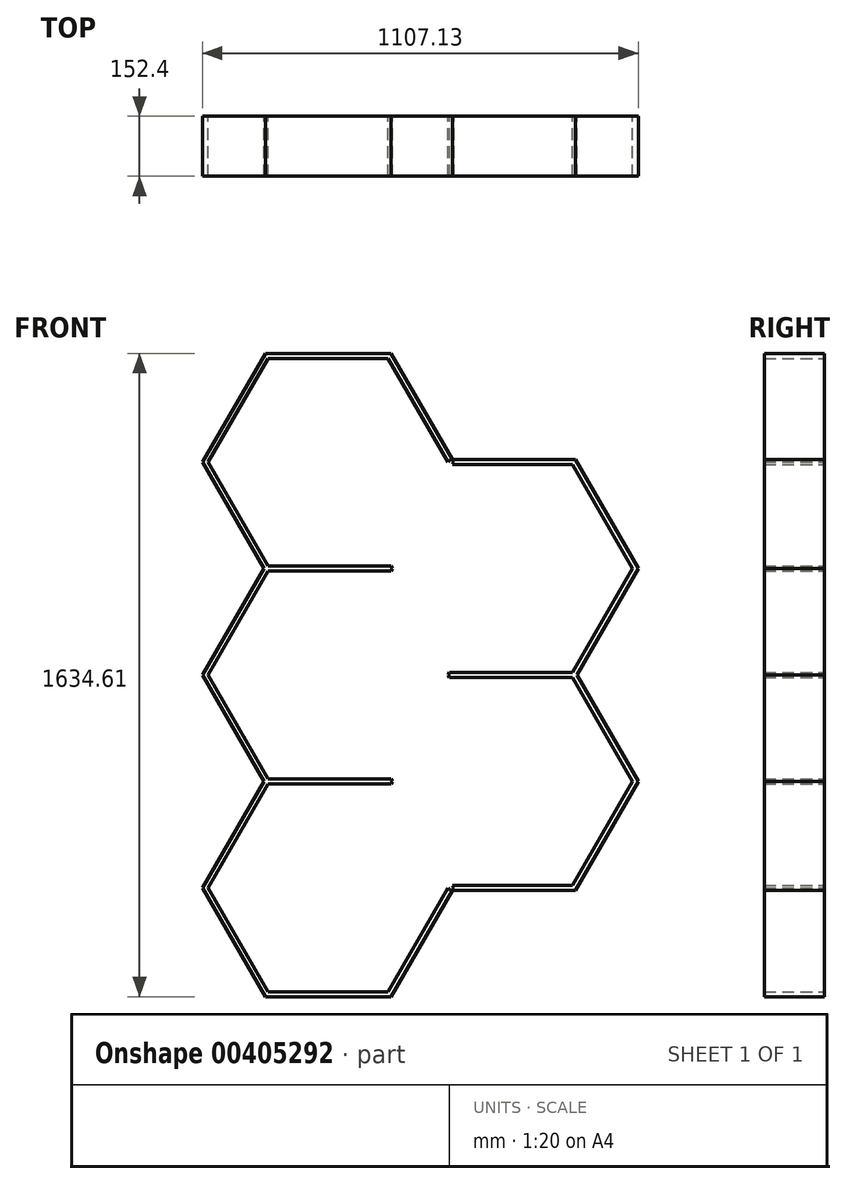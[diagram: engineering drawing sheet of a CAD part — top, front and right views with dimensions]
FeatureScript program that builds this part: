
annotation { "Feature Type Name" : "Feature", "Feature Type Description" : "" }
export const myFeature = defineFeature(function(context is Context, id is Id, definition is map)
    precondition{}
    {
        {
            var Q0;
            Q0=qCreatedBy(makeId("Front.planeOp"),FACE);
            var sketch = newSketch(context, id + "F0", { "sketchPlane" : qUnion([Q0])});
            skLineSegment(sketch, "E0.0", {"start": v(113.5, -269) * mm, "end": v(-191.3, -269) * mm});
            skLineSegment(sketch, "E0.1", {"start": v(-191.3, -269) * mm, "end": v(-343.7, -5.03) * mm});
            skLineSegment(sketch, "E0.2", {"start": v(-343.7, -5.03) * mm, "end": v(-191.3, 258.93) * mm});
            skLineSegment(sketch, "E0.3", {"start": v(-191.3, 258.93) * mm, "end": v(113.5, 258.93) * mm});
            skLineSegment(sketch, "E0.4", {"start": v(113.5, 258.93) * mm, "end": v(265.9, -5.03) * mm});
            skLineSegment(sketch, "E0.5", {"start": v(265.9, -5.03) * mm, "end": v(113.5, -269) * mm});
            skPoint(sketch, "E0.0.midPoint", {"position": v(-38.9, -269) * mm});
            skLineSegment(sketch, "E1.0", {"start": v(-358.37, -5.03) * mm, "end": v(-198.64, 271.63) * mm});
            skLineSegment(sketch, "E1.1", {"start": v(120.83, 271.63) * mm, "end": v(280.56, -5.03) * mm});
            skLineSegment(sketch, "E1.2", {"start": v(280.56, -5.03) * mm, "end": v(120.83, -281.7) * mm});
            skLineSegment(sketch, "E1.3", {"start": v(-198.64, 271.63) * mm, "end": v(120.83, 271.63) * mm});
            skLineSegment(sketch, "E1.4", {"start": v(120.83, -281.7) * mm, "end": v(-198.64, -281.7) * mm});
            skLineSegment(sketch, "E1.5", {"start": v(-198.64, -281.7) * mm, "end": v(-358.37, -5.03) * mm});
            skLineSegment(sketch, "E2.0.1.0", {"start": v(-191.3, 271.64) * mm, "end": v(-343.7, 535.6) * mm});
            skLineSegment(sketch, "E2.0.1.1", {"start": v(280.56, 535.6) * mm, "end": v(120.83, 258.94) * mm});
            skLineSegment(sketch, "E2.0.1.2", {"start": v(113.5, 271.64) * mm, "end": v(-191.3, 271.64) * mm});
            skLineSegment(sketch, "E2.0.1.3", {"start": v(120.83, 812.27) * mm, "end": v(280.56, 535.6) * mm});
            skLineSegment(sketch, "E2.0.1.4", {"start": v(265.9, 535.6) * mm, "end": v(113.5, 271.64) * mm});
            skPoint(sketch, "E2.0.1.5", {"position": v(-38.9, 271.64) * mm});
            skLineSegment(sketch, "E2.0.1.6", {"start": v(-358.37, 535.6) * mm, "end": v(-198.64, 812.27) * mm});
            skLineSegment(sketch, "E2.0.1.7", {"start": v(113.5, 799.57) * mm, "end": v(265.9, 535.6) * mm});
            skLineSegment(sketch, "E2.0.1.8", {"start": v(-198.64, 258.94) * mm, "end": v(-358.37, 535.6) * mm});
            skLineSegment(sketch, "E2.0.1.9", {"start": v(-191.3, 799.57) * mm, "end": v(113.5, 799.57) * mm});
            skLineSegment(sketch, "E2.0.1.10", {"start": v(120.83, 258.94) * mm, "end": v(-198.64, 258.94) * mm});
            skLineSegment(sketch, "E2.0.1.11", {"start": v(-343.7, 535.6) * mm, "end": v(-191.3, 799.57) * mm});
            skLineSegment(sketch, "E2.0.1.12", {"start": v(-198.64, 812.27) * mm, "end": v(120.83, 812.27) * mm});
            skLineSegment(sketch, "E2.0.2.0", {"start": v(-191.3, 812.28) * mm, "end": v(-343.7, 1076.24) * mm});
            skLineSegment(sketch, "E2.0.2.1", {"start": v(280.56, 1076.24) * mm, "end": v(120.83, 799.58) * mm});
            skLineSegment(sketch, "E2.0.2.2", {"start": v(113.5, 812.28) * mm, "end": v(-191.3, 812.28) * mm});
            skLineSegment(sketch, "E2.0.2.3", {"start": v(120.83, 1352.9) * mm, "end": v(280.56, 1076.24) * mm});
            skLineSegment(sketch, "E2.0.2.4", {"start": v(265.9, 1076.24) * mm, "end": v(113.5, 812.28) * mm});
            skPoint(sketch, "E2.0.2.5", {"position": v(-38.9, 812.28) * mm});
            skLineSegment(sketch, "E2.0.2.6", {"start": v(-358.37, 1076.24) * mm, "end": v(-198.64, 1352.9) * mm});
            skLineSegment(sketch, "E2.0.2.7", {"start": v(113.5, 1340.2) * mm, "end": v(265.9, 1076.24) * mm});
            skLineSegment(sketch, "E2.0.2.8", {"start": v(-198.64, 799.58) * mm, "end": v(-358.37, 1076.24) * mm});
            skLineSegment(sketch, "E2.0.2.9", {"start": v(-191.3, 1340.2) * mm, "end": v(113.5, 1340.2) * mm});
            skLineSegment(sketch, "E2.0.2.10", {"start": v(120.83, 799.58) * mm, "end": v(-198.64, 799.58) * mm});
            skLineSegment(sketch, "E2.0.2.11", {"start": v(-343.7, 1076.24) * mm, "end": v(-191.3, 1340.2) * mm});
            skLineSegment(sketch, "E2.0.2.12", {"start": v(-198.64, 1352.9) * mm, "end": v(120.83, 1352.9) * mm});
            skLineSegment(sketch, "E2.direction1", {"start": v(-358.37, -5.03) * mm, "end": v(-332.97, -5.03) * mm, "construction": true});
            skLineSegment(sketch, "E2.direction2", {"start": v(-358.37, -5.03) * mm, "end": v(-358.37, 535.6) * mm, "construction": true});
            skLineSegment(sketch, "E3.0", {"start": v(581.7, 1.32) * mm, "end": v(276.9, 1.32) * mm});
            skLineSegment(sketch, "E3.1", {"start": v(276.9, 1.32) * mm, "end": v(124.5, 265.28) * mm});
            skLineSegment(sketch, "E3.2", {"start": v(124.5, 265.28) * mm, "end": v(276.9, 529.25) * mm});
            skLineSegment(sketch, "E3.3", {"start": v(276.9, 529.25) * mm, "end": v(581.7, 529.25) * mm});
            skLineSegment(sketch, "E3.4", {"start": v(581.7, 529.25) * mm, "end": v(734.1, 265.28) * mm});
            skLineSegment(sketch, "E3.5", {"start": v(734.1, 265.28) * mm, "end": v(581.7, 1.32) * mm});
            skPoint(sketch, "E3.0.midPoint", {"position": v(429.3, 1.32) * mm});
            skLineSegment(sketch, "E4.0", {"start": v(109.83, 265.28) * mm, "end": v(269.56, 541.95) * mm});
            skLineSegment(sketch, "E4.1", {"start": v(589.02, 541.95) * mm, "end": v(748.76, 265.28) * mm});
            skLineSegment(sketch, "E4.2", {"start": v(748.76, 265.28) * mm, "end": v(589.02, -11.38) * mm});
            skLineSegment(sketch, "E4.3", {"start": v(269.56, 541.95) * mm, "end": v(589.02, 541.95) * mm});
            skLineSegment(sketch, "E4.4", {"start": v(589.02, -11.38) * mm, "end": v(269.56, -11.38) * mm});
            skLineSegment(sketch, "E4.5", {"start": v(269.56, -11.38) * mm, "end": v(109.83, 265.28) * mm});
            skLineSegment(sketch, "E5.0.1.0", {"start": v(276.9, 541.96) * mm, "end": v(124.5, 805.92) * mm});
            skLineSegment(sketch, "E5.0.1.1", {"start": v(748.76, 805.92) * mm, "end": v(589.02, 529.26) * mm});
            skLineSegment(sketch, "E5.0.1.2", {"start": v(581.7, 541.96) * mm, "end": v(276.9, 541.96) * mm});
            skLineSegment(sketch, "E5.0.1.3", {"start": v(589.02, 1082.59) * mm, "end": v(748.76, 805.92) * mm});
            skLineSegment(sketch, "E5.0.1.4", {"start": v(734.1, 805.92) * mm, "end": v(581.7, 541.96) * mm});
            skPoint(sketch, "E5.0.1.5", {"position": v(510.77, 548) * mm});
            skLineSegment(sketch, "E5.0.1.6", {"start": v(109.83, 805.92) * mm, "end": v(269.56, 1082.59) * mm});
            skLineSegment(sketch, "E5.0.1.7", {"start": v(581.7, 1069.89) * mm, "end": v(734.1, 805.92) * mm});
            skLineSegment(sketch, "E5.0.1.8", {"start": v(269.56, 529.26) * mm, "end": v(109.83, 805.92) * mm});
            skLineSegment(sketch, "E5.0.1.9", {"start": v(276.9, 1069.89) * mm, "end": v(581.7, 1069.89) * mm});
            skLineSegment(sketch, "E5.0.1.10", {"start": v(589.02, 529.26) * mm, "end": v(269.56, 529.26) * mm});
            skLineSegment(sketch, "E5.0.1.11", {"start": v(124.5, 805.92) * mm, "end": v(276.9, 1069.89) * mm});
            skLineSegment(sketch, "E5.0.1.12", {"start": v(269.56, 1082.59) * mm, "end": v(589.02, 1082.59) * mm});
            skPoint(sketch, "E5.0.2.5", {"position": v(510.77, 1088.64) * mm});
            skLineSegment(sketch, "E5.direction1", {"start": v(109.83, 271.32) * mm, "end": v(135.23, 271.32) * mm, "construction": true});
            skPoint(sketch, "E6", {"position": v(124.5, 265.28) * mm});
            skPoint(sketch, "E7", {"position": v(124.5, 805.92) * mm});
            skPoint(sketch, "E8", {"position": v(265.9, 535.6) * mm});
            skLineSegment(sketch, "E9", {"start": v(269.56, 541.95) * mm, "end": v(269.56, 529.26) * mm, "construction": true});
            skLineSegment(sketch, "E10", {"start": v(276.9, 541.96) * mm, "end": v(276.9, 529.25) * mm, "construction": true});
            skLineSegment(sketch, "E11", {"start": v(581.7, 1069.89) * mm, "end": v(276.9, 1.32) * mm, "construction": true});
            skLineSegment(sketch, "E12", {"start": v(276.9, 1069.89) * mm, "end": v(581.7, 1.32) * mm, "construction": true});
            skLineSegment(sketch, "E13", {"start": v(748.76, 265.28) * mm, "end": v(109.83, 805.92) * mm, "construction": true});
            skLineSegment(sketch, "E14", {"start": v(748.76, 805.92) * mm, "end": v(109.83, 265.28) * mm, "construction": true});
            skSolve(sketch);
        }
        {
            var Q0;
            Q0=makeQuery(id+"F0.imprint","IMPRINT",FACE,{"disambiguationData":[TD([[makeQuery(id+"F0.imprint","IMPRINT",EDGE,{"derivedFrom":sQuery(id+"F0.wireOp",EDGE,"E2.0.2.0")}),1.0]])]});
            var Q1;
            {var subQ5=sQuery(id+"F0.wireOp",EDGE,"E1.0");var subQ7=sQuery(id+"F0.wireOp",EDGE,"E1.3");var subQ8=makeQuery(id+"F0.imprint","INTERSECT",VERTEX,{"derivedFrom":[subQ5,subQ7]});Q1=makeQuery(id+"F0.imprint","IMPRINT",FACE,{"disambiguationData":[TD([[makeQuery(id+"F0.imprint","IMPRINT",EDGE,{"disambiguationData":[TD([[subQ8,1.0]])],"derivedFrom":subQ5}),-1.0]])]});}
            var Q2;
            {var subQ5=sQuery(id+"F0.wireOp",EDGE,"E2.0.1.6");var subQ7=sQuery(id+"F0.wireOp",EDGE,"E2.0.1.12");var subQ8=makeQuery(id+"F0.imprint","INTERSECT",VERTEX,{"derivedFrom":[subQ5,subQ7]});Q2=makeQuery(id+"F0.imprint","IMPRINT",FACE,{"disambiguationData":[TD([[makeQuery(id+"F0.imprint","IMPRINT",EDGE,{"disambiguationData":[TD([[subQ8,1.0]])],"derivedFrom":subQ5}),-1.0]])]});}
            var Q3;
            Q3=makeQuery(id+"F0.imprint","IMPRINT",FACE,{"disambiguationData":[TD([[makeQuery(id+"F0.imprint","IMPRINT",EDGE,{"derivedFrom":sQuery(id+"F0.wireOp",EDGE,"E2.0.1.0")}),1.0]])]});
            var Q4;
            {var subQ11=sQuery(id+"F0.wireOp",EDGE,"E3.1");Q4=makeQuery(id+"F0.imprint","IMPRINT",FACE,{"disambiguationData":[TD([[makeQuery(id+"F0.imprint","IMPRINT",EDGE,{"derivedFrom":subQ11}),1.0]])]});}
            var Q5;
            {var subQ8=sQuery(id+"F0.wireOp",EDGE,"E5.0.1.0");Q5=makeQuery(id+"F0.imprint","IMPRINT",FACE,{"disambiguationData":[TD([[makeQuery(id+"F0.imprint","IMPRINT",EDGE,{"derivedFrom":subQ8}),1.0]])]});}
            var Q6;
            {var subQ5=sQuery(id+"F0.wireOp",EDGE,"E2.0.1.3");var subQ6=sQuery(id+"F0.wireOp",EDGE,"E2.0.1.1");var subQ7=makeQuery(id+"F0.imprint","INTERSECT",VERTEX,{"derivedFrom":[subQ6,subQ5]});Q6=makeQuery(id+"F0.imprint","IMPRINT",FACE,{"disambiguationData":[TD([[makeQuery(id+"F0.imprint","IMPRINT",EDGE,{"disambiguationData":[TD([[subQ7,-1.0]])],"derivedFrom":subQ6}),-1.0]])]});}
            var Q7;
            {var subQ10=sQuery(id+"F0.wireOp",EDGE,"E3.0");Q7=makeQuery(id+"F0.imprint","IMPRINT",FACE,{"disambiguationData":[TD([[makeQuery(id+"F0.imprint","IMPRINT",EDGE,{"derivedFrom":subQ10}),1.0]])]});}
            var Q8;
            {var subQ0=sQuery(id+"F0.wireOp",EDGE,"E3.2");Q8=makeQuery(id+"F0.imprint","IMPRINT",FACE,{"disambiguationData":[TD([[makeQuery(id+"F0.imprint","IMPRINT",EDGE,{"derivedFrom":subQ0}),1.0]])]});}
            var Q9;
            {var subQ5=sQuery(id+"F0.wireOp",EDGE,"E1.1");var subQ7=sQuery(id+"F0.wireOp",EDGE,"E1.3");var subQ8=makeQuery(id+"F0.imprint","INTERSECT",VERTEX,{"derivedFrom":[subQ5,subQ7]});Q9=makeQuery(id+"F0.imprint","IMPRINT",FACE,{"disambiguationData":[TD([[makeQuery(id+"F0.imprint","IMPRINT",EDGE,{"disambiguationData":[TD([[subQ8,1.0]])],"derivedFrom":subQ7}),-1.0]])]});}
            var Q10;
            Q10=makeQuery(id+"F0.imprint","IMPRINT",FACE,{"disambiguationData":[TD([[makeQuery(id+"F0.imprint","IMPRINT",EDGE,{"derivedFrom":sQuery(id+"F0.wireOp",EDGE,"E0.0")}),1.0]])]});
            var Q11;
            {var subQ5=sQuery(id+"F0.wireOp",EDGE,"E5.0.1.11");Q11=makeQuery(id+"F0.imprint","IMPRINT",FACE,{"disambiguationData":[TD([[makeQuery(id+"F0.imprint","IMPRINT",EDGE,{"derivedFrom":subQ5}),1.0]])]});}
            var Q12;
            {var subQ5=sQuery(id+"F0.wireOp",EDGE,"E2.0.1.3");var subQ7=sQuery(id+"F0.wireOp",EDGE,"E2.0.1.1");var subQ8=makeQuery(id+"F0.imprint","INTERSECT",VERTEX,{"derivedFrom":[subQ7,subQ5]});Q12=makeQuery(id+"F0.imprint","IMPRINT",FACE,{"disambiguationData":[TD([[makeQuery(id+"F0.imprint","IMPRINT",EDGE,{"disambiguationData":[TD([[subQ8,-1.0]])],"derivedFrom":subQ7}),1.0]])]});}
            var Q13;
            {var subQ5=sQuery(id+"F0.wireOp",EDGE,"E2.0.1.12");var subQ6=sQuery(id+"F0.wireOp",EDGE,"E2.0.1.3");var subQ7=makeQuery(id+"F0.imprint","INTERSECT",VERTEX,{"derivedFrom":[subQ6,subQ5]});Q13=makeQuery(id+"F0.imprint","IMPRINT",FACE,{"disambiguationData":[TD([[makeQuery(id+"F0.imprint","IMPRINT",EDGE,{"disambiguationData":[TD([[subQ7,1.0]])],"derivedFrom":subQ5}),-1.0]])]});}
            var Q14;
            {var subQ0=sQuery(id+"F0.wireOp",EDGE,"E5.0.1.2");Q14=makeQuery(id+"F0.imprint","IMPRINT",FACE,{"disambiguationData":[TD([[makeQuery(id+"F0.imprint","IMPRINT",EDGE,{"derivedFrom":subQ0}),1.0]])]});}
            extrude(context, id + "F1", {"entities" : qUnion([Q0, Q1, Q2, Q3, Q4, Q5, Q6, Q7, Q8, Q9, Q10, Q11, Q12, Q13, Q14]), "depth" : 152.4 * mm});
        }
    });
